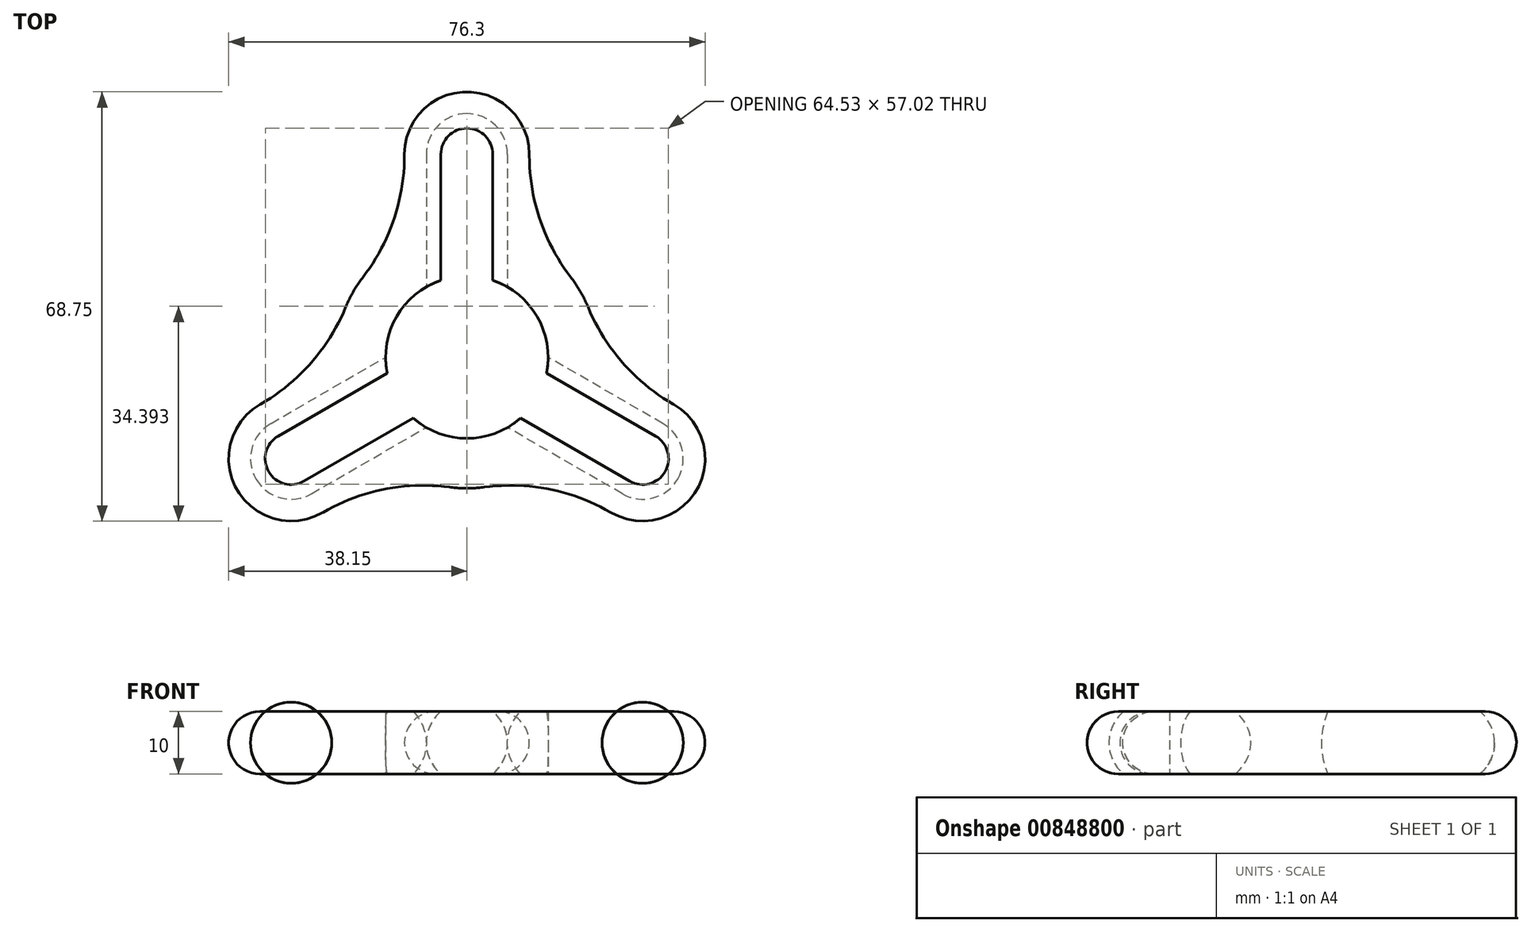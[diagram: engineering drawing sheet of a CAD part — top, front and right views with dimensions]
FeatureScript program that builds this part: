
annotation { "Feature Type Name" : "Feature", "Feature Type Description" : "" }
export const myFeature = defineFeature(function(context is Context, id is Id, definition is map)
    precondition{}
    {
        {
            var Q0;
            Q0=qCreatedBy(makeId("Top.planeOp"),FACE);
            var sketch = newSketch(context, id + "F0", { "sketchPlane" : qUnion([Q0])});
            skCircle(sketch, "E0", {"center": v(0, 0) * mm, "radius": 13 * mm});
            skArc(sketch, "E1", {"start": v(10, 18.47) * mm, "mid": v(0, -21) * mm, "end": v(-10, 18.47) * mm});
            skLineSegment(sketch, "E2.top", {"start": v(10, 42.5) * mm, "end": v(-10, 42.5) * mm});
            skLineSegment(sketch, "E2.left", {"start": v(10, 18.47) * mm, "end": v(10, 42.5) * mm});
            skLineSegment(sketch, "E2.right", {"start": v(-10, 18.47) * mm, "end": v(-10, 42.5) * mm});
            skPoint(sketch, "E2.middle", {"position": v(0, -0.36) * mm});
            skPoint(sketch, "E3.orphan", {"position": v(-10, -43.21) * mm});
            skPoint(sketch, "E4.orphan", {"position": v(10, -43.21) * mm});
            skSolve(sketch);
        }
        {
            var Q0;
            Q0=makeQuery(id+"F0.imprint","IMPRINT",FACE,{"disambiguationData":[TD([[makeQuery(id+"F0.imprint","IMPRINT",EDGE,{"derivedFrom":sQuery(id+"F0.wireOp",EDGE,"E0")}),-1.0]])]});
            extrude(context, id + "F1", {"entities" : qUnion([Q0]), "depth" : 10 * mm, "offsetDistance" : 25 * mm, "symmetric" : true});
        }
        {
            var Q0;
            Q0=makeQuery(id+"F1.opExtrude","CAP_FACE",FACE,{"disambiguationData":[OSD([sQuery(id+"F0.wireOp",EDGE,"E0"),sQuery(id+"F0.wireOp",EDGE,"E1"),sQuery(id+"F0.wireOp",EDGE,"E2.top"),sQuery(id+"F0.wireOp",EDGE,"E2.left"),sQuery(id+"F0.wireOp",EDGE,"E2.right")])],"isStart":false});
            var sketch = newSketch(context, id + "F2", { "sketchPlane" : qUnion([Q0])});
            skLineSegment(sketch, "E5", {"start": v(0, 0) * mm, "end": v(0, 38.1) * mm, "construction": true});
            skLineSegment(sketch, "E6", {"start": v(0, 0) * mm, "end": v(29.6, 15.08) * mm});
            skPoint(sketch, "E7.end.orphan", {"position": v(-28.2, 18.47) * mm});
            skLineSegment(sketch, "E8", {"start": v(29.6, 15.08) * mm, "end": v(29.6, -30.55) * mm});
            skLineSegment(sketch, "E9", {"start": v(29.6, -30.55) * mm, "end": v(0, -30.55) * mm});
            skLineSegment(sketch, "E10.MirrorCS", {"start": v(0, 0) * mm, "end": v(-29.6, 15.08) * mm});
            skLineSegment(sketch, "E11.MirrorCS", {"start": v(-29.6, 15.08) * mm, "end": v(-29.6, -30.55) * mm});
            skLineSegment(sketch, "E12.MirrorCS", {"start": v(-29.6, -30.55) * mm, "end": v(0, -30.55) * mm});
            skSolve(sketch);
        }
        {
            var Q0;
            {var subQ5=sQuery(id+"F2.wireOp",EDGE,"E8");Q0=makeQuery(id+"F2.imprint","IMPRINT",FACE,{"disambiguationData":[TD([[makeQuery(id+"F2.imprint","IMPRINT",EDGE,{"derivedFrom":subQ5}),-1.0]])]});}
            var Q1;
            {var subQ0=sQuery(id+"F2.wireOp",EDGE,"E6");var subQ1=makeQuery(id+"F1.opExtrude","CAP_EDGE",EDGE,{"disambiguationData":[OSD([sQuery(id+"F0.wireOp",EDGE,"E1")])],"isStart":false});var subQ2=makeQuery(id+"F2.imprint","INTERSECT",VERTEX,{"derivedFrom":[subQ1,subQ0]});Q1=makeQuery(id+"F2.imprint","IMPRINT",FACE,{"disambiguationData":[TD([[makeQuery(id+"F2.imprint","IMPRINT",EDGE,{"disambiguationData":[TD([[subQ2,1.0]])],"derivedFrom":subQ0}),-1.0]])]});}
            var Q2;
            {var subQ0=sQuery(id+"F2.wireOp",EDGE,"E10.MirrorCS");var subQ1=sQuery(id+"F2.wireOp",EDGE,"E6");var subQ2=makeQuery(id+"F2.imprint","INTERSECT",VERTEX,{"derivedFrom":[subQ1,subQ0]});Q2=makeQuery(id+"F2.imprint","IMPRINT",FACE,{"disambiguationData":[TD([[makeQuery(id+"F2.imprint","IMPRINT",EDGE,{"disambiguationData":[TD([[subQ2,-1.0]])],"derivedFrom":subQ1}),-1.0]])]});}
            extrude(context, id + "F3", {"entities" : qUnion([Q0, Q1, Q2]), "operationType" : NewBodyOperationType.REMOVE, "oppositeDirection" : true, "depth" : 25 * mm, "offsetDistance" : 25 * mm});
        }
        {
            var Q0;
            Q0=makeQuery(id+"F1.opExtrude","SWEPT_EDGE",EDGE,{"disambiguationData":[OSD([sQuery(id+"F0.wireOp",EDGE,"E2.top"),sQuery(id+"F0.wireOp",EDGE,"E2.left")])]});
            var Q1;
            Q1=makeQuery(id+"F1.opExtrude","SWEPT_EDGE",EDGE,{"disambiguationData":[OSD([sQuery(id+"F0.wireOp",EDGE,"E2.top"),sQuery(id+"F0.wireOp",EDGE,"E2.right")])]});
            fillet(context, id + "F4", {"entities" : qUnion([Q0, Q1]), "radius" : 10 * mm, "tangentPropagation" : true, "allowEdgeOverflow" : false});
        }
        {
            var Q0;
            Q0=makeQuery(id+"F1.opExtrude","SWEPT_EDGE",EDGE,{"disambiguationData":[OSD([sQuery(id+"F0.wireOp",EDGE,"E1"),sQuery(id+"F0.wireOp",EDGE,"E2.left")])]});
            var Q1;
            Q1=makeQuery(id+"F1.opExtrude","SWEPT_EDGE",EDGE,{"disambiguationData":[OSD([sQuery(id+"F0.wireOp",EDGE,"E1"),sQuery(id+"F0.wireOp",EDGE,"E2.right")])]});
            fillet(context, id + "F5", {"entities" : qUnion([Q0, Q1]), "radius" : 32 * mm, "tangentPropagation" : true, "allowEdgeOverflow" : false});
        }
        {
            var Q0;
            Q0=qCreatedBy(makeId("Front.planeOp"),FACE);
            var sketch = newSketch(context, id + "F6", { "sketchPlane" : qUnion([Q0])});
            skCircle(sketch, "E13", {"center": v(0, 0) * mm, "radius": 6.5 * mm});
            skSolve(sketch);
        }
        {
            var Q0;
            Q0 = qSketchRegion(id + "F6", true);
            extrude(context, id + "F7", {"entities" : qUnion([Q0]), "oppositeDirection" : true, "depth" : 39 * mm, "offsetDistance" : 25 * mm, "hasSecondDirection" : true, "secondDirectionOppositeDirection" : true, "secondDirectionDepth" : 3 * mm});
        }
        {
            var Q0;
            Q0=makeQuery(id+"F7.opExtrude","CAP_EDGE",EDGE,{"disambiguationData":[OSD([sQuery(id+"F6.wireOp",EDGE,"E13")])],"isStart":false});
            var Q1;
            Q1=makeQuery(id+"F7.opExtrude","CAP_EDGE",EDGE,{"disambiguationData":[OSD([sQuery(id+"F6.wireOp",EDGE,"E13")])],"isStart":true});
            fillet(context, id + "F8", {"entities" : qUnion([Q0, Q1]), "radius" : 6.5 * mm, "tangentPropagation" : true, "allowEdgeOverflow" : false});
        }
        {
            var Q0;
            Q0=makeQuery(id+"F7.opExtrude","SWEPT_BODY",BODY,{"disambiguationData":[OSD([sQuery(id+"F6.wireOp",EDGE,"E13")])]});
            var Q1;
            Q1=makeQuery(id+"F1.opExtrude","SWEPT_BODY",BODY,{"disambiguationData":[OSD([sQuery(id+"F0.wireOp",EDGE,"E0"),sQuery(id+"F0.wireOp",EDGE,"E1"),sQuery(id+"F0.wireOp",EDGE,"E2.top"),sQuery(id+"F0.wireOp",EDGE,"E2.left"),sQuery(id+"F0.wireOp",EDGE,"E2.right")])]});
            booleanBodies(context, id + "F9", {"operationType" : BooleanOperationType.SUBTRACTION, "tools" : qUnion([Q0]), "targets" : qUnion([Q1])});
        }
        {
            var Q0;
            Q0=makeQuery(id+"F1.opExtrude","SWEPT_BODY",BODY,{"disambiguationData":[OSD([sQuery(id+"F0.wireOp",EDGE,"E0"),sQuery(id+"F0.wireOp",EDGE,"E1"),sQuery(id+"F0.wireOp",EDGE,"E2.top"),sQuery(id+"F0.wireOp",EDGE,"E2.left"),sQuery(id+"F0.wireOp",EDGE,"E2.right")])]});
            var Q1;
            {var subQ4=sQuery(id+"F0.wireOp",EDGE,"E0");Q1=makeQuery(id+"F9.opBoolean","SPLIT",FACE,{"disambiguationData":[TD([makeQuery(id+"F3.boolean.opBoolean","COPY",FACE,{"derivedFrom":makeQuery(id+"F3.opExtrude","SWEPT_FACE",FACE,{"disambiguationData":[OSD([sQuery(id+"F2.wireOp",EDGE,"E10.MirrorCS")])]})})])],"derivedFrom":makeQuery(id+"F1.opExtrude","SWEPT_FACE",FACE,{"disambiguationData":[OSD([subQ4])]})});}
            circularPattern(context, id + "F10", {"operationType" : NewBodyOperationType.ADD, "entities" : qUnion([Q0]), "axis" : qUnion([Q1]), "angle" : 360 * degree, "instanceCount" : 3, "equalSpace" : true, "computeTransformsWithoutBuiltin" : true});
        }
        {
            var Q0;
            Q0=makeQuery(id+"F10.opPattern","COPY",EDGE,{"derivedFrom":makeQuery(id+"F1.opExtrude","CAP_EDGE",EDGE,{"disambiguationData":[OSD([sQuery(id+"F0.wireOp",EDGE,"E2.left")])],"isStart":false}),"instanceName":"2"});
            var Q1;
            Q1=makeQuery(id+"F10.opPattern","COPY",EDGE,{"derivedFrom":makeQuery(id+"F1.opExtrude","CAP_EDGE",EDGE,{"disambiguationData":[OSD([sQuery(id+"F0.wireOp",EDGE,"E2.left")])],"isStart":true}),"instanceName":"2"});
            fillet(context, id + "F11", {"entities" : qUnion([Q0, Q1]), "radius" : 5 * mm, "tangentPropagation" : true, "allowEdgeOverflow" : false});
        }
        {
            var Q0;
            {var subQ0=makeQuery(id+"F1.opExtrude","CAP_FACE",FACE,{"disambiguationData":[OSD([sQuery(id+"F0.wireOp",EDGE,"E0"),sQuery(id+"F0.wireOp",EDGE,"E1"),sQuery(id+"F0.wireOp",EDGE,"E2.top"),sQuery(id+"F0.wireOp",EDGE,"E2.left"),sQuery(id+"F0.wireOp",EDGE,"E2.right")])],"isStart":false});Q0=makeQuery(id+"F10.boolean.opBoolean","MERGE",FACE,{"derivedFrom":[subQ0,makeQuery(id+"F10.opPattern","COPY",FACE,{"derivedFrom":subQ0,"instanceName":"1"}),makeQuery(id+"F10.opPattern","COPY",FACE,{"derivedFrom":subQ0,"instanceName":"2"})]});}
            var sketch = newSketch(context, id + "F12", { "sketchPlane" : qUnion([Q0])});
            skCircle(sketch, "E14", {"center": v(0, 0) * mm, "radius": 13 * mm});
            skSolve(sketch);
        }
        {
            var Q0;
            {var subQ0=sQuery(id+"F12.wireOp",EDGE,"E14");var subQ1=makeQuery(id+"Fc30LF1fgpgI4RY_1.boolean.opBoolean","COPY",EDGE,{"derivedFrom":makeQuery(id+"Fc30LF1fgpgI4RY_1.opExtrude","CAP_EDGE",EDGE,{"disambiguationData":[OSD([sQuery(id+"F29CxmzKmEXTXxc_1.wireOp",EDGE,"011db73b-9863-401d-bd6c-c5530aa96b7a.0")])],"isStart":true})});var subQ6=makeQuery(id+"F12.imprint","INTERSECT",VERTEX,{"derivedFrom":[subQ1,subQ0]});Q0=makeQuery(id+"F12.imprint","IMPRINT",FACE,{"disambiguationData":[TD([[makeQuery(id+"F12.imprint","IMPRINT",EDGE,{"disambiguationData":[TD([[subQ6,1.0]])],"derivedFrom":subQ0}),1.0]])]});}
            extrude(context, id + "F13", {"entities" : qUnion([Q0]), "operationType" : NewBodyOperationType.REMOVE, "oppositeDirection" : true, "depth" : 25 * mm, "offsetDistance" : 25 * mm});
        }
    });
